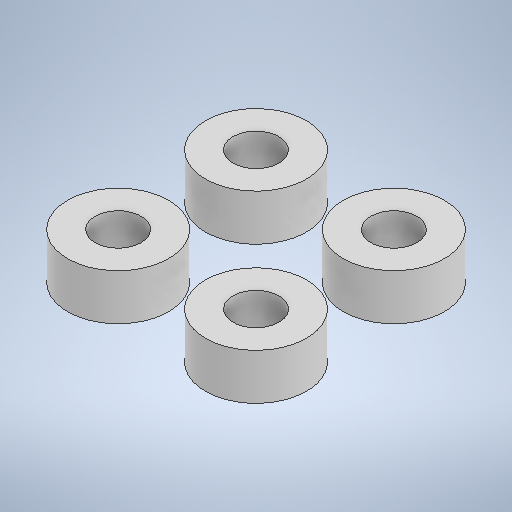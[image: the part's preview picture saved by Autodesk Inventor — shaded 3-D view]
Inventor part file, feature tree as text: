
AUTODESK INVENTOR PART (.ipt)
format: ipt  version: 2025.1 (Build 291241000, 241)  size: 251,904 bytes
history: native  units: in
note: dims shown in document units (in); Inventor stores cm internally (conversion verified against a paired STEP export)
features: extrude x1, sketch x1
ambient origin geometry x8: Origin, YZ Plane, XZ Plane, XY Plane, X Axis, Y Axis, Z Axis, Center Point
bodies: Solid1 (feature_tree)
feature tree (2):
  extrude  "Extrusion1"  Depth=0.2953in
  sketch  "Sketch1"  dims[d0=0.4331in d1=0.2953in d2=0.1969in d3=0.2953in d4=0.1969in d5=0.0in]
